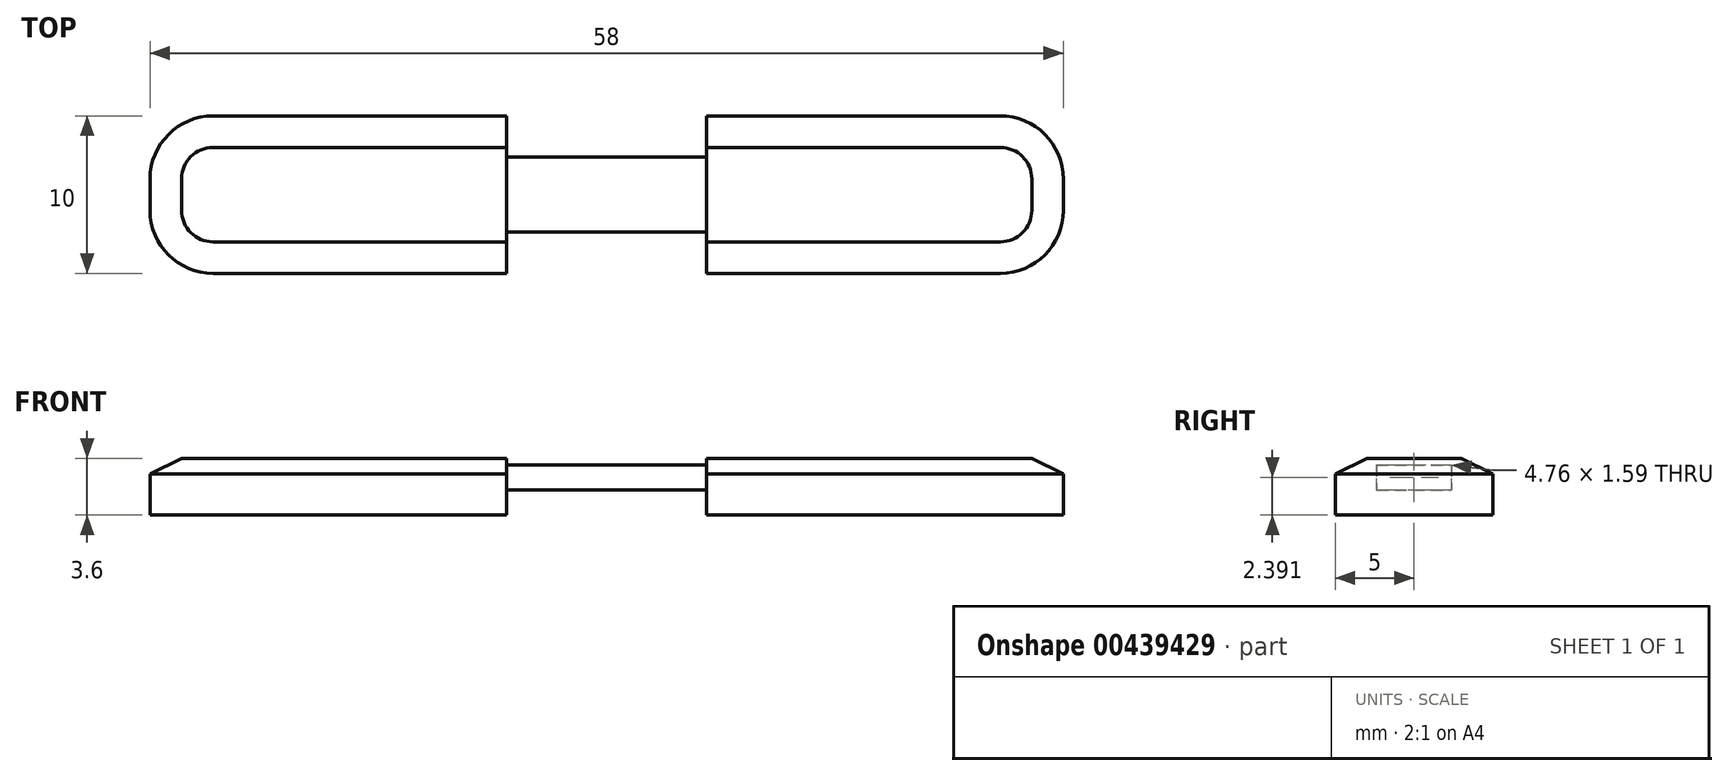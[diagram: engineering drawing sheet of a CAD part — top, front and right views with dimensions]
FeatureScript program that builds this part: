
annotation { "Feature Type Name" : "Feature", "Feature Type Description" : "" }
export const myFeature = defineFeature(function(context is Context, id is Id, definition is map)
    precondition{}
    {
        {
            var Q0;
            Q0=qCreatedBy(makeId("Top.planeOp"),FACE);
            var sketch = newSketch(context, id + "F0", { "sketchPlane" : qUnion([Q0])});
            skLineSegment(sketch, "E0.bottom", {"start": v(29, 5) * mm, "end": v(-29, 5) * mm});
            skLineSegment(sketch, "E0.top", {"start": v(29, -5) * mm, "end": v(-29, -5) * mm});
            skLineSegment(sketch, "E0.left", {"start": v(29, 5) * mm, "end": v(29, -5) * mm});
            skLineSegment(sketch, "E0.right", {"start": v(-29, 5) * mm, "end": v(-29, -5) * mm});
            skPoint(sketch, "E0.middle", {"position": v(0, 0) * mm});
            skLineSegment(sketch, "E1", {"start": v(0, -5) * mm, "end": v(0, 5) * mm, "construction": true});
            skSolve(sketch);
        }
        {
            var Q0;
            Q0=qSketchRegion(id+"F0",true);
            extrude(context, id + "F1", {"entities" : qUnion([Q0]), "depth" : 1.6 * mm});
        }
        {
            var Q0;
            Q0=makeQuery(id+"F1.opExtrude","CAP_FACE",FACE,{"disambiguationData":[OSD([sQuery(id+"F0.wireOp",EDGE,"E0.bottom"),sQuery(id+"F0.wireOp",EDGE,"E0.top"),sQuery(id+"F0.wireOp",EDGE,"E0.left"),sQuery(id+"F0.wireOp",EDGE,"E0.right"),sQuery(id+"F0.wireOp",EDGE,"sQ5FOiL1-PATm-f4FL-sMBU-Sejo3Ob4zhOJ.top"),sQuery(id+"F0.wireOp",EDGE,"eE3g78Th-Uhqz-HL4B-METg-kGSabsW8tSUq"),sQuery(id+"F0.wireOp",EDGE,"LGPMkXvS-dz4y-Jq5w-iaXi-xn5e82dF6vV4"),sQuery(id+"F0.wireOp",EDGE,"e5298548-960a-4d00-80d0-4a68bccc32c3.trimOffspring")])],"isStart":false});
            var sketch = newSketch(context, id + "F2", { "sketchPlane" : qUnion([Q0])});
            skLineSegment(sketch, "E2.bottom", {"start": v(-7.94, 2.38) * mm, "end": v(7.94, 2.38) * mm});
            skLineSegment(sketch, "E2.top", {"start": v(-7.94, -2.38) * mm, "end": v(7.94, -2.38) * mm});
            skLineSegment(sketch, "E2.left", {"start": v(-7.94, 2.38) * mm, "end": v(-7.94, -2.38) * mm});
            skLineSegment(sketch, "E2.right", {"start": v(7.94, 2.38) * mm, "end": v(7.94, -2.38) * mm});
            skPoint(sketch, "E2.middle", {"position": v(0, 0) * mm});
            skSolve(sketch);
        }
        {
            var Q0;
            Q0=qSketchRegion(id+"F2",true);
            extrude(context, id + "F3", {"entities" : qUnion([Q0]), "operationType" : NewBodyOperationType.ADD, "depth" : 1.59 * mm});
        }
        {
            var Q0;
            Q0=makeQuery(id+"F3.opExtrude","CAP_FACE",FACE,{"disambiguationData":[OSD([sQuery(id+"F2.wireOp",EDGE,"E2.bottom"),sQuery(id+"F2.wireOp",EDGE,"E2.top"),sQuery(id+"F2.wireOp",EDGE,"E2.left"),sQuery(id+"F2.wireOp",EDGE,"E2.right")])],"isStart":false});
            cPlane(context, id + "F4", {"entities" : qUnion([Q0]), "cplaneType" : CPlaneType.OFFSET, "offset" : 0.8 * mm, "oppositeDirection" : true, "width" : 152.4 * mm, "height" : 152.4 * mm});
        }
        {
            var Q0;
            Q0=qCreatedBy(id+"F4.planeOp",FACE);
            var sketch = newSketch(context, id + "F5", { "sketchPlane" : qUnion([Q0])});
            skLineSegment(sketch, "E3.0.1", {"start": v(-6.35, -2.38) * mm, "end": v(6.35, -2.38) * mm});
            skLineSegment(sketch, "E3.0.3", {"start": v(6.35, 2.38) * mm, "end": v(-6.35, 2.38) * mm});
            skLineSegment(sketch, "E4", {"start": v(-6.35, 2.38) * mm, "end": v(-6.35, -2.38) * mm});
            skLineSegment(sketch, "E5", {"start": v(6.35, 2.38) * mm, "end": v(6.35, -2.38) * mm});
            skLineSegment(sketch, "E6", {"start": v(0, 2.38) * mm, "end": v(0, -2.38) * mm, "construction": true});
            skSolve(sketch);
        }
        {
            var Q0;
            Q0=qSketchRegion(id+"F5",true);
            var Q1;
            Q1=makeQuery(id+"F1.opExtrude","CAP_FACE",FACE,{"disambiguationData":[OSD([sQuery(id+"F0.wireOp",EDGE,"E0.bottom"),sQuery(id+"F0.wireOp",EDGE,"E0.top"),sQuery(id+"F0.wireOp",EDGE,"E0.left"),sQuery(id+"F0.wireOp",EDGE,"E0.right"),sQuery(id+"F0.wireOp",EDGE,"sQ5FOiL1-PATm-f4FL-sMBU-Sejo3Ob4zhOJ.top"),sQuery(id+"F0.wireOp",EDGE,"eE3g78Th-Uhqz-HL4B-METg-kGSabsW8tSUq"),sQuery(id+"F0.wireOp",EDGE,"LGPMkXvS-dz4y-Jq5w-iaXi-xn5e82dF6vV4"),sQuery(id+"F0.wireOp",EDGE,"e5298548-960a-4d00-80d0-4a68bccc32c3.trimOffspring")])],"isStart":true});
            extrude(context, id + "F6", {"entities" : qUnion([Q0]), "operationType" : NewBodyOperationType.REMOVE, "endBound" : BoundingType.UP_TO_SURFACE, "oppositeDirection" : true, "endBoundEntityFace" : qUnion([Q1]), "depth" : 0.8 * mm});
        }
        {
            var Q0;
            Q0=makeQuery(id+"F1.opExtrude","CAP_FACE",FACE,{"disambiguationData":[OSD([sQuery(id+"F0.wireOp",EDGE,"E0.bottom"),sQuery(id+"F0.wireOp",EDGE,"E0.top"),sQuery(id+"F0.wireOp",EDGE,"E0.left"),sQuery(id+"F0.wireOp",EDGE,"E0.right"),sQuery(id+"F0.wireOp",EDGE,"sQ5FOiL1-PATm-f4FL-sMBU-Sejo3Ob4zhOJ.top"),sQuery(id+"F0.wireOp",EDGE,"eE3g78Th-Uhqz-HL4B-METg-kGSabsW8tSUq"),sQuery(id+"F0.wireOp",EDGE,"LGPMkXvS-dz4y-Jq5w-iaXi-xn5e82dF6vV4"),sQuery(id+"F0.wireOp",EDGE,"e5298548-960a-4d00-80d0-4a68bccc32c3.trimOffspring")])],"isStart":false});
            var sketch = newSketch(context, id + "F7", { "sketchPlane" : qUnion([Q0])});
            skLineSegment(sketch, "E7.bottom", {"start": v(-6.35, -2.38) * mm, "end": v(6.35, -2.38) * mm});
            skLineSegment(sketch, "E7.top", {"start": v(-6.35, -5) * mm, "end": v(6.35, -5) * mm});
            skLineSegment(sketch, "E7.left", {"start": v(-6.35, -2.38) * mm, "end": v(-6.35, -5) * mm});
            skLineSegment(sketch, "E7.right", {"start": v(6.35, -2.38) * mm, "end": v(6.35, -5) * mm});
            skSolve(sketch);
        }
        {
            var Q0;
            Q0=qSketchRegion(id+"F7",true);
            extrude(context, id + "F8", {"entities" : qUnion([Q0]), "operationType" : NewBodyOperationType.REMOVE, "endBound" : BoundingType.THROUGH_ALL, "oppositeDirection" : true, "depth" : 25 * mm});
        }
        {
            var Q0;
            Q0=makeQuery(id+"F1.opExtrude","CAP_FACE",FACE,{"disambiguationData":[OSD([sQuery(id+"F0.wireOp",EDGE,"E0.bottom"),sQuery(id+"F0.wireOp",EDGE,"E0.top"),sQuery(id+"F0.wireOp",EDGE,"E0.left"),sQuery(id+"F0.wireOp",EDGE,"E0.right"),sQuery(id+"F0.wireOp",EDGE,"sQ5FOiL1-PATm-f4FL-sMBU-Sejo3Ob4zhOJ.top"),sQuery(id+"F0.wireOp",EDGE,"eE3g78Th-Uhqz-HL4B-METg-kGSabsW8tSUq"),sQuery(id+"F0.wireOp",EDGE,"LGPMkXvS-dz4y-Jq5w-iaXi-xn5e82dF6vV4"),sQuery(id+"F0.wireOp",EDGE,"e5298548-960a-4d00-80d0-4a68bccc32c3.trimOffspring")])],"isStart":false});
            var sketch = newSketch(context, id + "F9", { "sketchPlane" : qUnion([Q0])});
            skLineSegment(sketch, "E8.bottom", {"start": v(-6.35, 2.38) * mm, "end": v(6.35, 2.38) * mm});
            skLineSegment(sketch, "E8.top", {"start": v(-6.35, 5) * mm, "end": v(6.35, 5) * mm});
            skLineSegment(sketch, "E8.left", {"start": v(-6.35, 2.38) * mm, "end": v(-6.35, 5) * mm});
            skLineSegment(sketch, "E8.right", {"start": v(6.35, 2.38) * mm, "end": v(6.35, 5) * mm});
            skSolve(sketch);
        }
        {
            var Q0;
            Q0=qSketchRegion(id+"F9",true);
            extrude(context, id + "F10", {"entities" : qUnion([Q0]), "operationType" : NewBodyOperationType.REMOVE, "endBound" : BoundingType.THROUGH_ALL, "oppositeDirection" : true, "depth" : 25 * mm});
        }
        {
            var Q0;
            Q0=makeQuery(id+"F6.boolean.opBoolean","COPY",FACE,{"derivedFrom":makeQuery(id+"F6.opExtrude","CAP_FACE",FACE,{"disambiguationData":[OSD([sQuery(id+"F5.wireOp",EDGE,"E3.0.1"),sQuery(id+"F5.wireOp",EDGE,"E3.0.3"),sQuery(id+"F5.wireOp",EDGE,"E4"),sQuery(id+"F5.wireOp",EDGE,"E5")])],"isStart":true})});
            var sketch = newSketch(context, id + "F11", { "sketchPlane" : qUnion([Q0])});
            skLineSegment(sketch, "E9.0.0", {"start": v(6.35, -2.38) * mm, "end": v(6.35, 2.38) * mm});
            skLineSegment(sketch, "E9.0.1", {"start": v(6.35, 2.38) * mm, "end": v(-6.35, 2.38) * mm});
            skLineSegment(sketch, "E9.0.2", {"start": v(-6.35, 2.38) * mm, "end": v(-6.35, -2.38) * mm});
            skLineSegment(sketch, "E9.0.3", {"start": v(-6.35, -2.38) * mm, "end": v(6.35, -2.38) * mm});
            skSolve(sketch);
        }
        {
            var Q0;
            Q0=qSketchRegion(id+"F11",true);
            extrude(context, id + "F12", {"entities" : qUnion([Q0]), "operationType" : NewBodyOperationType.ADD, "depth" : 0.8 * mm});
        }
        {
            var Q0;
            {var subQ0=sQuery(id+"F0.wireOp",EDGE,"E0.top");var subQ1=sQuery(id+"F0.wireOp",EDGE,"E0.right");var subQ2=sQuery(id+"F0.wireOp",EDGE,"E0.bottom");Q0=makeQuery(id+"F10.boolean.opBoolean","SPLIT",FACE,{"disambiguationData":[TD([makeQuery(id+"F1.opExtrude","SWEPT_FACE",FACE,{"disambiguationData":[OSD([subQ1])]})])],"derivedFrom":makeQuery(id+"F1.opExtrude","CAP_FACE",FACE,{"disambiguationData":[OSD([subQ2,subQ0,sQuery(id+"F0.wireOp",EDGE,"E0.left"),subQ1])],"isStart":false})});}
            var sketch = newSketch(context, id + "F13", { "sketchPlane" : qUnion([Q0])});
            skLineSegment(sketch, "E10.0", {"start": v(-29, 5) * mm, "end": v(-29, -5) * mm});
            skLineSegment(sketch, "E11.0", {"start": v(-6.35, -5) * mm, "end": v(-29, -5) * mm});
            skLineSegment(sketch, "E12.0", {"start": v(-6.35, 5) * mm, "end": v(-29, 5) * mm});
            skLineSegment(sketch, "E13.0", {"start": v(29, -5) * mm, "end": v(6.35, -5) * mm});
            skLineSegment(sketch, "E14.0", {"start": v(29, 5) * mm, "end": v(29, -5) * mm});
            skLineSegment(sketch, "E15.0", {"start": v(29, 5) * mm, "end": v(6.35, 5) * mm});
            skLineSegment(sketch, "E16", {"start": v(-6.35, 5) * mm, "end": v(-6.35, -5) * mm});
            skLineSegment(sketch, "E17", {"start": v(6.35, 5) * mm, "end": v(6.35, -5) * mm});
            skSolve(sketch);
        }
        {
            var Q0;
            Q0 = qSketchRegion(id + "F13", true);
            extrude(context, id + "F14", {"entities" : qUnion([Q0]), "operationType" : NewBodyOperationType.ADD, "depth" : 2 * mm});
        }
        {
            var Q0;
            Q0=makeQuery(id+"F1.opExtrude","SWEPT_EDGE",EDGE,{"disambiguationData":[OSD([sQuery(id+"F0.wireOp",EDGE,"E0.top"),sQuery(id+"F0.wireOp",EDGE,"E0.right")])]});
            var Q1;
            Q1=makeQuery(id+"F1.opExtrude","SWEPT_EDGE",EDGE,{"disambiguationData":[OSD([sQuery(id+"F0.wireOp",EDGE,"E0.top"),sQuery(id+"F0.wireOp",EDGE,"E0.left")])]});
            var Q2;
            Q2=makeQuery(id+"F1.opExtrude","SWEPT_EDGE",EDGE,{"disambiguationData":[OSD([sQuery(id+"F0.wireOp",EDGE,"E0.bottom"),sQuery(id+"F0.wireOp",EDGE,"E0.left")])]});
            var Q3;
            Q3=makeQuery(id+"F1.opExtrude","SWEPT_EDGE",EDGE,{"disambiguationData":[OSD([sQuery(id+"F0.wireOp",EDGE,"sQ5FOiL1-PATm-f4FL-sMBU-Sejo3Ob4zhOJ.top"),sQuery(id+"F0.wireOp",EDGE,"LGPMkXvS-dz4y-Jq5w-iaXi-xn5e82dF6vV4")])]});
            var Q4;
            Q4=makeQuery(id+"F1.opExtrude","SWEPT_EDGE",EDGE,{"disambiguationData":[OSD([sQuery(id+"F0.wireOp",EDGE,"E0.right"),sQuery(id+"F0.wireOp",EDGE,"e5298548-960a-4d00-80d0-4a68bccc32c3.trimOffspring")])]});
            var Q5;
            Q5=makeQuery(id+"F1.opExtrude","SWEPT_EDGE",EDGE,{"disambiguationData":[OSD([sQuery(id+"F0.wireOp",EDGE,"sQ5FOiL1-PATm-f4FL-sMBU-Sejo3Ob4zhOJ.top"),sQuery(id+"F0.wireOp",EDGE,"eE3g78Th-Uhqz-HL4B-METg-kGSabsW8tSUq")])]});
            var Q6;
            Q6=makeQuery(id+"F1.opExtrude","SWEPT_EDGE",EDGE,{"disambiguationData":[OSD([sQuery(id+"F0.wireOp",EDGE,"eE3g78Th-Uhqz-HL4B-METg-kGSabsW8tSUq"),sQuery(id+"F0.wireOp",EDGE,"e5298548-960a-4d00-80d0-4a68bccc32c3.trimOffspring")])]});
            var Q7;
            Q7=makeQuery(id+"F1.opExtrude","SWEPT_EDGE",EDGE,{"disambiguationData":[OSD([sQuery(id+"F0.wireOp",EDGE,"E0.bottom"),sQuery(id+"F0.wireOp",EDGE,"LGPMkXvS-dz4y-Jq5w-iaXi-xn5e82dF6vV4")])]});
            fillet(context, id + "F15", {"entities" : qUnion([Q0, Q1, Q2, Q3, Q4, Q5, Q6, Q7]), "radius" : 4 * mm, "tangentPropagation" : true, "allowEdgeOverflow" : false});
        }
        {
            var Q0;
            Q0=makeQuery(id+"F14.opExtrude","CAP_EDGE",EDGE,{"disambiguationData":[OSD([sQuery(id+"F13.wireOp",EDGE,"E11.0")])],"isStart":false});
            var Q1;
            Q1=makeQuery(id+"F14.opExtrude","CAP_EDGE",EDGE,{"disambiguationData":[OSD([sQuery(id+"F13.wireOp",EDGE,"E13.0")])],"isStart":false});
            chamfer(context, id + "F16", {"entities" : qUnion([Q0, Q1]), "chamferType" : ChamferType.TWO_OFFSETS, "width1" : 2 * mm, "oppositeDirection" : true, "width2" : 1 * mm, "tangentPropagation" : true});
        }
    });
